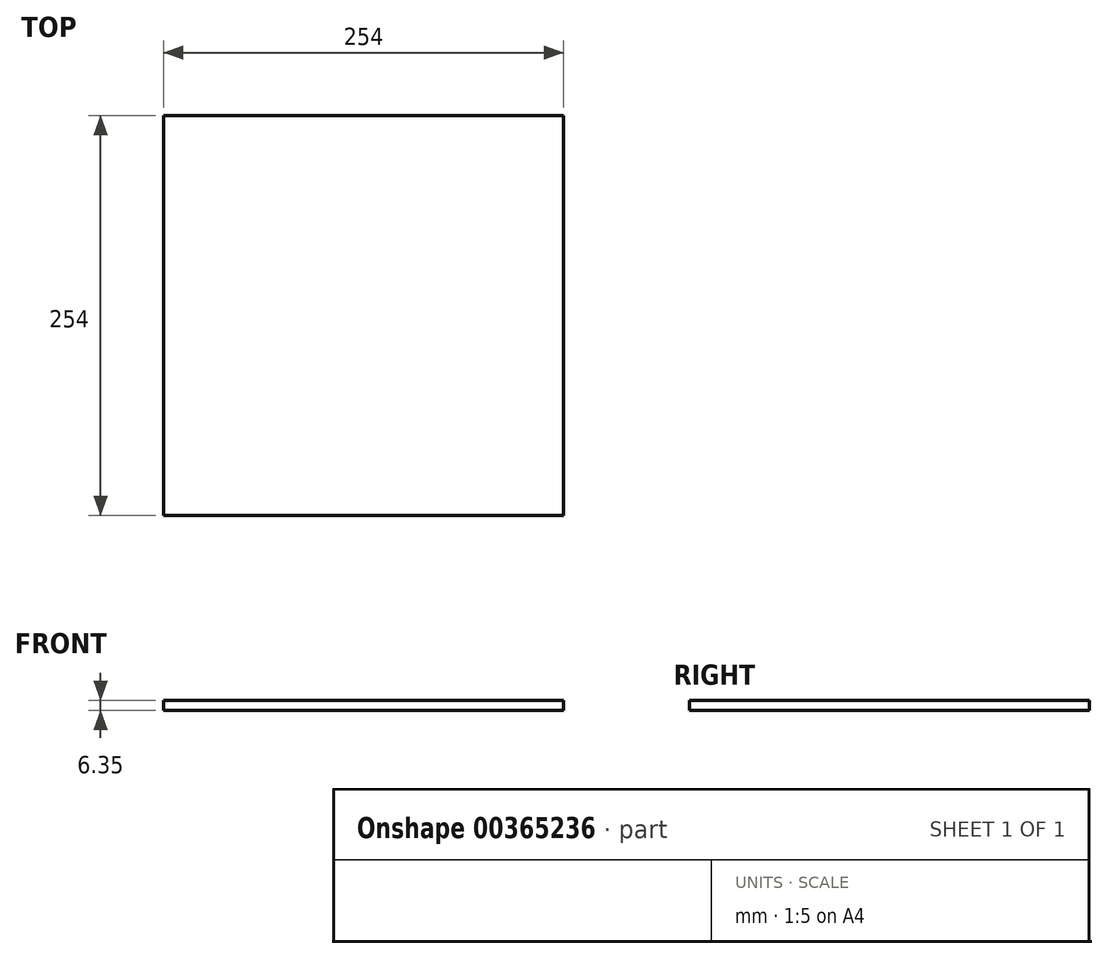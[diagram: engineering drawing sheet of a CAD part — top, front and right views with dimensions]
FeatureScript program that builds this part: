
annotation { "Feature Type Name" : "Feature", "Feature Type Description" : "" }
export const myFeature = defineFeature(function(context is Context, id is Id, definition is map)
    precondition{}
    {
        {
            var Q0;
            Q0=qCreatedBy(makeId("Top.planeOp"),FACE);
            var sketch = newSketch(context, id + "F0", { "sketchPlane" : qUnion([Q0])});
            skLineSegment(sketch, "E0.bottom", {"start": v(0, 0) * mm, "end": v(254, 0) * mm});
            skLineSegment(sketch, "E0.top", {"start": v(0, 254) * mm, "end": v(254, 254) * mm});
            skLineSegment(sketch, "E0.left", {"start": v(0, 0) * mm, "end": v(0, 254) * mm});
            skLineSegment(sketch, "E0.right", {"start": v(254, 0) * mm, "end": v(254, 254) * mm});
            skSolve(sketch);
        }
        {
            var Q0;
            Q0 = qSketchRegion(id + "F0", true);
            extrude(context, id + "F1", {"entities" : qUnion([Q0]), "depth" : 6.35 * mm, "offsetDistance" : 25.4 * mm});
        }
    });
